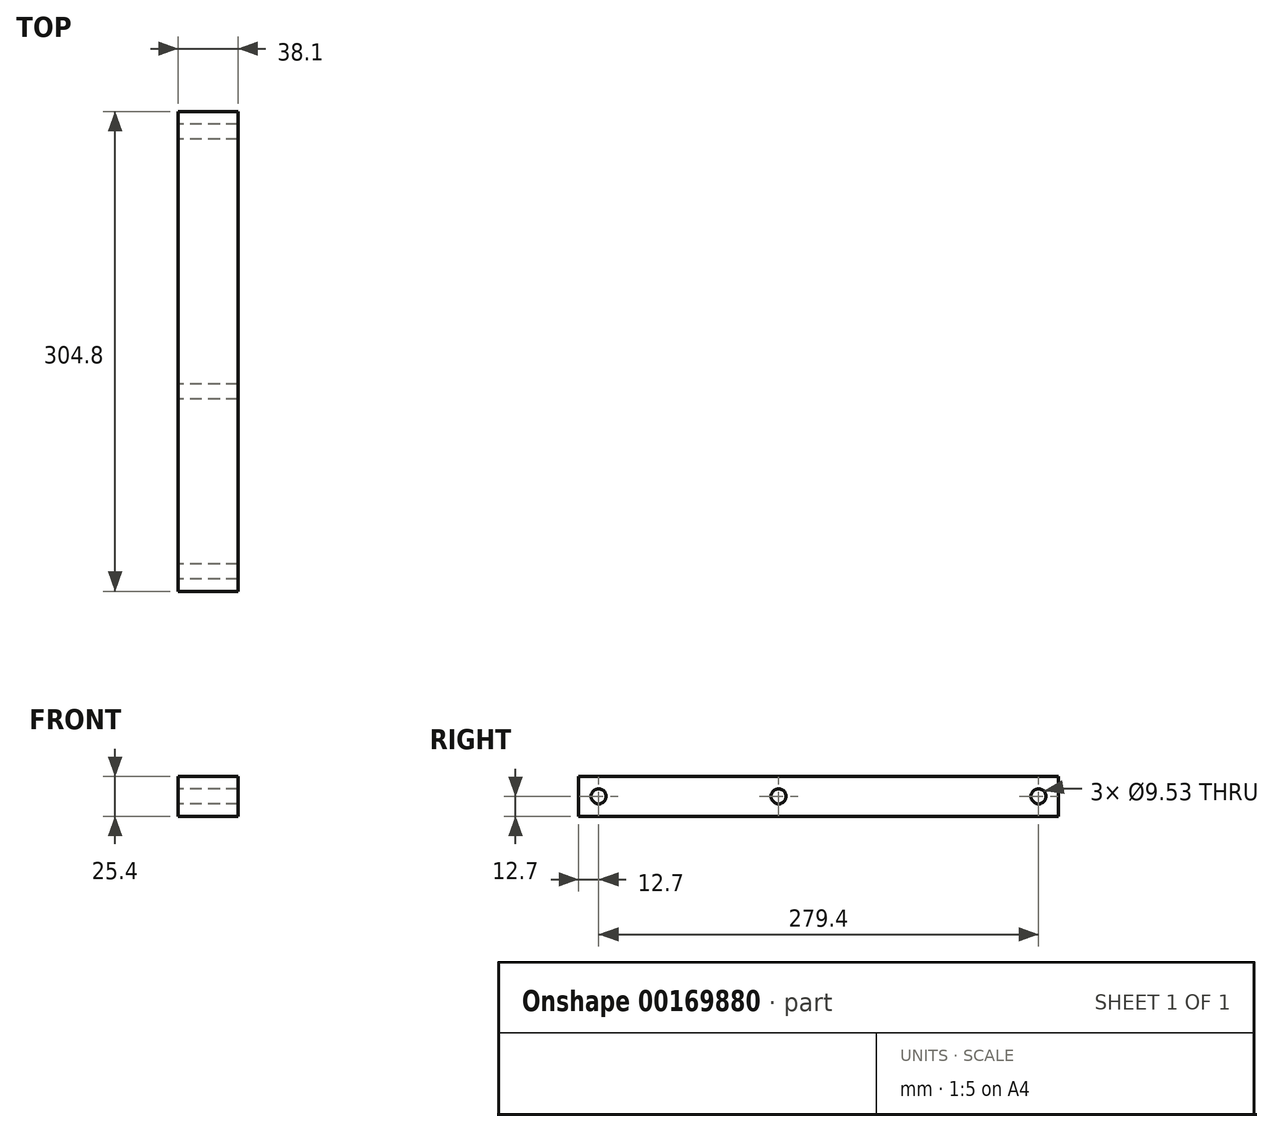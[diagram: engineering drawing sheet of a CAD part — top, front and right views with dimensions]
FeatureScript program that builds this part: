
annotation { "Feature Type Name" : "Feature", "Feature Type Description" : "" }
export const myFeature = defineFeature(function(context is Context, id is Id, definition is map)
    precondition{}
    {
        {
            var Q0;
            Q0=qCreatedBy(makeId("Right.planeOp"),FACE);
            var sketch = newSketch(context, id + "F0", { "sketchPlane" : qUnion([Q0])});
            skLineSegment(sketch, "E0.bottom", {"start": v(-127, 12.7) * mm, "end": v(0, 12.7) * mm});
            skLineSegment(sketch, "E0.top", {"start": v(-127, -12.7) * mm, "end": v(0, -12.7) * mm});
            skLineSegment(sketch, "E0.left", {"start": v(-127, 12.7) * mm, "end": v(-127, -12.7) * mm});
            skLineSegment(sketch, "E0.right", {"start": v(0, 12.7) * mm, "end": v(0, -12.7) * mm});
            skLineSegment(sketch, "E1.bottom", {"start": v(0, 12.7) * mm, "end": v(177.8, 12.7) * mm});
            skLineSegment(sketch, "E1.top", {"start": v(0, -12.7) * mm, "end": v(177.8, -12.7) * mm});
            skLineSegment(sketch, "E1.right", {"start": v(177.8, 12.7) * mm, "end": v(177.8, -12.7) * mm});
            skLineSegment(sketch, "E2", {"start": v(-127, 0) * mm, "end": v(0, 0) * mm, "construction": true});
            skLineSegment(sketch, "E3", {"start": v(0, 0) * mm, "end": v(177.8, 0) * mm, "construction": true});
            skCircle(sketch, "E4", {"center": v(-114.3, 0) * mm, "radius": 4.76 * mm});
            skCircle(sketch, "E5", {"center": v(0, 0) * mm, "radius": 4.76 * mm});
            skCircle(sketch, "E6", {"center": v(165.1, 0) * mm, "radius": 4.76 * mm});
            skSolve(sketch);
        }
        {
            var Q0;
            Q0 = qSketchRegion(id + "F0", true);
            extrude(context, id + "F1", {"entities" : qUnion([Q0]), "depth" : 38.1 * mm});
        }
        {
            var Q0;
            Q0 = qSketchRegion(id + "F0", true);
            extrude(context, id + "F2", {"entities" : qUnion([Q0]), "operationType" : NewBodyOperationType.ADD, "depth" : 25.4 * mm});
        }
    });
